# Revit family: BM 3362 Chair Linen webbing
name_source: partatom
category: Furniture
revit_build: Autodesk Revit 2017 (Build: 20171027_0315(x64)
units: mm (PartAtom-declared; Revit-internal decimal feet)

## family parameters
Always vertical = Yes
Cut with Voids When Loaded = No
OmniClass Number = 23.40.20.00
OmniClass Title = General Furniture and Specialties
Room Calculation Point = No
Shared = No
Work Plane-Based = No

## types (1)
- BM 3362 Chair Linen webbing
    Armrest = FF Oak Soap horizontal
    Backrest and Seat Modify Materials = Change Backrest & Seat Materials in Mange -> Object Styles->Imported objects
    Depth = 48 cm
    Description = The BM62/BM61 is done in a slender and elegant construction of solid wood with back and seat weaved in either cane wicker or linen webbing.  The back is slightly curved making it an excellent dinning chair that offers the possibility to sit upright during a dinner and relaxing back into the chair for many hours afterwards.
    Design year = 1957
    Frame Horizontal = FF Oak Soap horizontal
    Frame Vertical = FF Oak Soap vertical
    Height = 76,5 cm
    Item No. = 3361
    Manufacturer = Fredericia Furniture
    Model = BM 3361 Chair Linen webbing
    Seat Height = 45,5 cm
    URL = https://www.fredericia.com
    Variations Frame = Available in other kind of wood
    Variations Seat - Backrest = Natural Linen webbing or Black Linen webbing
    Width = 48 cm

## geometry (parser evidence)
native form markers: Sweep x2
no freeform markers — native parametric forms only
